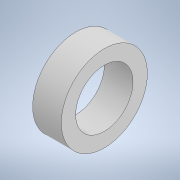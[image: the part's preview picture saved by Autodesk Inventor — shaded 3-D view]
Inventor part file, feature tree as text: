
AUTODESK INVENTOR PART (.ipt)
format: ipt  version: 2022 (Build 260153070, 153G)  size: 103,936 bytes
history: native  units: mm
features: extrude x2, sketch x2
ambient origin geometry x8: Origin, YZ Plane, XZ Plane, XY Plane, X Axis, Y Axis, Z Axis, Center Point
bodies: Solid1 (feature_tree)
feature tree (4):
  extrude  "Extrusion1"  Depth=1.0mm TaperAngle=0.0deg
  extrude  "Extrusion2"  Depth=1.0mm TaperAngle=0.0deg
  sketch  "Sketch1"  dims[d0=3.0mm d1=1.0mm d2=0.0mm]
  sketch  "Sketch2"  dims[d3=2.0mm d4=1.0mm d5=0.0mm]
